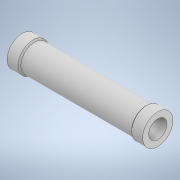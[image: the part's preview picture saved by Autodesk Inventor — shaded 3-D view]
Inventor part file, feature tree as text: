
AUTODESK INVENTOR PART (.ipt)
format: ipt  version: 2021 (Build 250183000, 183)  size: 112,128 bytes
history: native  units: mm
features: revolve x1, sketch x1
ambient origin geometry x8: Origin, YZ Plane, XZ Plane, XY Plane, X Axis, Y Axis, Z Axis, Center Point
bodies: Solid1 (feature_tree)
feature tree (2):
  revolve  "Revolution1"  [1 undecoded]
  sketch  "Sketch1"  dims[d0=3.3mm d1=40.4mm d2=49.4mm d3=0.5mm d4=5.0mm d5=90.0deg]
note: 1 required parameter value undecoded (feature->parameter linkage not recoverable at this tier; creation-order binding heuristic only, values carry confidence <= 0.55)
